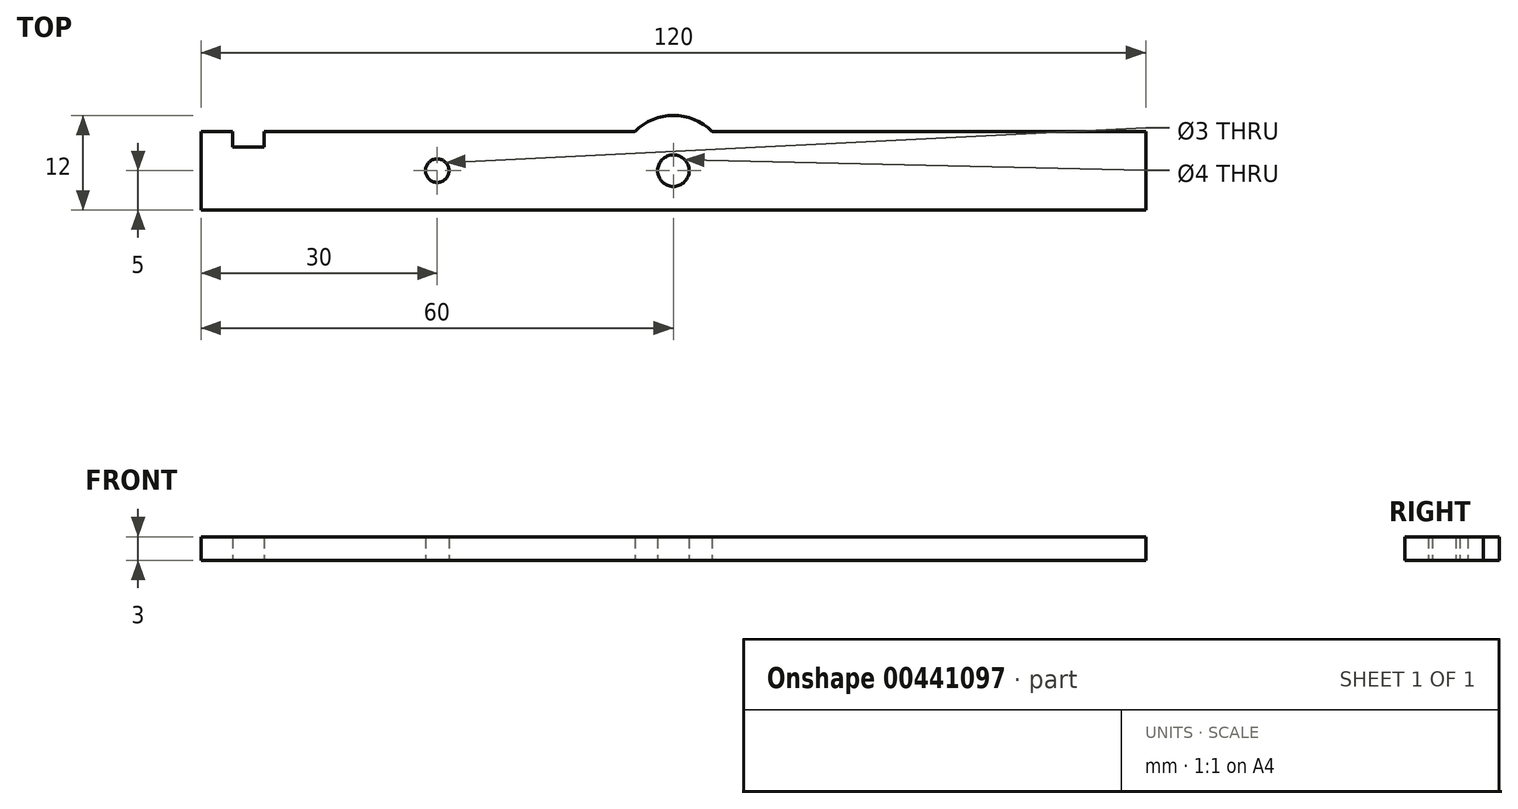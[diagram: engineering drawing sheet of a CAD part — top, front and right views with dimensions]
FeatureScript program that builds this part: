
annotation { "Feature Type Name" : "Feature", "Feature Type Description" : "" }
export const myFeature = defineFeature(function(context is Context, id is Id, definition is map)
    precondition{}
    {
        {
            var Q0;
            Q0=qCreatedBy(makeId("Top.planeOp"),FACE);
            var sketch = newSketch(context, id + "F0", { "sketchPlane" : qUnion([Q0])});
            skLineSegment(sketch, "E0.bottom", {"start": v(60, -5) * mm, "end": v(-60, -5) * mm});
            skLineSegment(sketch, "E0.top", {"start": v(60, 5) * mm, "end": v(-60, 5) * mm});
            skLineSegment(sketch, "E0.left", {"start": v(60, -5) * mm, "end": v(60, 5) * mm});
            skLineSegment(sketch, "E0.right", {"start": v(-60, -5) * mm, "end": v(-60, 5) * mm});
            skPoint(sketch, "E0.middle", {"position": v(0, 0) * mm});
            skCircle(sketch, "E1", {"center": v(0, 0) * mm, "radius": 7 * mm});
            skCircle(sketch, "E2", {"center": v(0, 0) * mm, "radius": 2 * mm});
            skLineSegment(sketch, "E3.bottom", {"start": v(-56, 5) * mm, "end": v(-52, 5) * mm});
            skLineSegment(sketch, "E3.top", {"start": v(-56, 3) * mm, "end": v(-52, 3) * mm});
            skLineSegment(sketch, "E3.left", {"start": v(-56, 5) * mm, "end": v(-56, 3) * mm});
            skLineSegment(sketch, "E3.right", {"start": v(-52, 5) * mm, "end": v(-52, 3) * mm});
            skCircle(sketch, "E4", {"center": v(-30, 0) * mm, "radius": 1.5 * mm});
            skSolve(sketch);
        }
        {
            var Q0;
            {var subQ0=sQuery(id+"F0.wireOp",EDGE,"E0.right");Q0=makeQuery(id+"F0.imprint","IMPRINT",FACE,{"disambiguationData":[TD([[makeQuery(id+"F0.imprint","IMPRINT",EDGE,{"derivedFrom":subQ0}),-1.0]])]});}
            var Q1;
            Q1=makeQuery(id+"F0.imprint","IMPRINT",FACE,{"disambiguationData":[TD([[makeQuery(id+"F0.imprint","IMPRINT",EDGE,{"derivedFrom":sQuery(id+"F0.wireOp",EDGE,"E2")}),-1.0]])]});
            var Q2;
            {var subQ0=sQuery(id+"F0.wireOp",EDGE,"E1");var subQ1=sQuery(id+"F0.wireOp",EDGE,"E0.top");var subQ2=makeQuery(id+"F0.imprint","INTERSECT",VERTEX,{"disambiguationData":[OD(0.0)],"derivedFrom":[subQ1,subQ0]});Q2=makeQuery(id+"F0.imprint","IMPRINT",FACE,{"disambiguationData":[TD([[makeQuery(id+"F0.imprint","IMPRINT",EDGE,{"disambiguationData":[TD([[subQ2,-1.0]])],"derivedFrom":subQ1}),-1.0]])]});}
            var Q3;
            {var subQ0=sQuery(id+"F0.wireOp",EDGE,"E1");var subQ1=sQuery(id+"F0.wireOp",EDGE,"E0.bottom");var subQ2=makeQuery(id+"F0.imprint","INTERSECT",VERTEX,{"disambiguationData":[OD(0.0)],"derivedFrom":[subQ1,subQ0]});Q3=makeQuery(id+"F0.imprint","IMPRINT",FACE,{"disambiguationData":[TD([[makeQuery(id+"F0.imprint","IMPRINT",EDGE,{"disambiguationData":[TD([[subQ2,-1.0]])],"derivedFrom":subQ1}),1.0]])]});}
            var Q4;
            {var subQ0=sQuery(id+"F0.wireOp",EDGE,"E0.left");Q4=makeQuery(id+"F0.imprint","IMPRINT",FACE,{"disambiguationData":[TD([[makeQuery(id+"F0.imprint","IMPRINT",EDGE,{"derivedFrom":subQ0}),1.0]])]});}
            extrude(context, id + "F1", {"entities" : qUnion([Q0, Q1, Q2, Q3, Q4]), "depth" : 3 * mm});
        }
    });
